# Revit family: Deca_Desviador para chuveiro_1982_1982
name_source: partatom
category: Plumbing Fixtures
units: mm (PartAtom-declared; Revit-internal decimal feet)

## family parameters
Cut with Voids When Loaded = No
Host = Face
Part Type = Normal
Room Calculation Point = No
Round Connector Dimension = Use Radius
Shared = No

## types (2) — shared parameters
Acompanha o Produto = Acompanha Parafuso e bucha para fixação
Aprovado por = quattroD
Atendimento ao Cliente = 0800-0117073
Categoria = CHUVEIROS E DUCHAS
Composição Anel Vedação = -
Composição Assento = -
Composição Básica = Liga cobre (bronze e latão),Aço,Plástico de Engenharia,Elastômeros
Composição Componente = -
Consumo = -
Cor Interna = -
Cor Secundária = -
Cores Componente = -
Criado por = quattroD
Código Pai = 1982
Default Elevation = 2200 mm
Description = Desviador para chuveiro
Diâmetro Água Fria = 15 mm
Informações Complementares = -
Itens de Instalação = -
Linha = Banho Competitivo
Manufacturer = Deca
Norma = Não Possui
Pressão máx. funcionamento = 40 MCA
Pressão mín. Aquec. Acúmulo = 4 MCA
Pressão mín. Aquec. Passagem = 4 MCA
Pressão mín. funcionamento = 4 MCA
Raio Água Fria = 8 mm  [stored 0.0262467 ft]
Saída de Esgoto = -
Segmento = Banheiro Competitivo
Tipo de dispositivo economizador = -
Tipo de mecanismo utilizado = -
Tipo de rosca de entrada = BSP NBR 8133
Tipo de rosca de saída = -
URL = www.deca.com.br
Vazão na Pressão máx. (L/min) = -
Vazão na Pressão mín. (L/min) = -

## per-type parameters (varying)
| type | Cor Principal | Material | Model | Peso Líquido (Kg) |
| 1982.C_Cromado | Cromado | Deca_Cromado | 1982.C | 0.663 |
| 1982.GL_Gold | Gold | Deca_Gold | 1982.GL | 1.107 |

note: [stored X ft] marks values corroborated as IEEE doubles in the binary element streams (Revit-internal decimal feet)

## geometry (parser evidence)
native form markers: Sweep x1
no freeform markers — native parametric forms only
